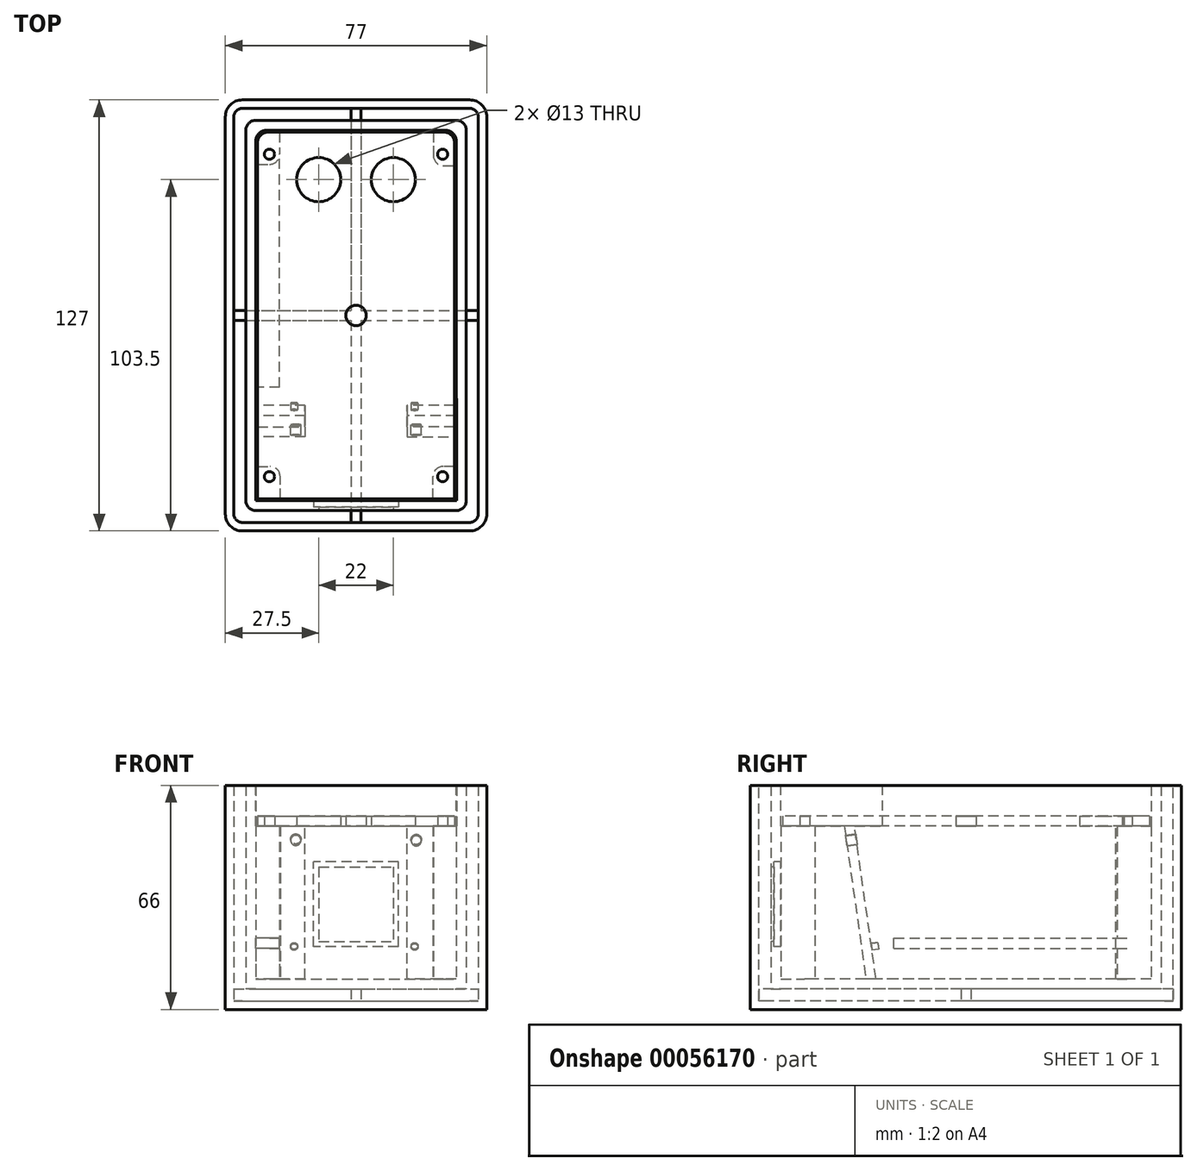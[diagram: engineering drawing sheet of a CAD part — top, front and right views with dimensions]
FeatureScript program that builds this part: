
annotation { "Feature Type Name" : "Feature", "Feature Type Description" : "" }
export const myFeature = defineFeature(function(context is Context, id is Id, definition is map)
    precondition{}
    {
        {
            var Q0;
            Q0=qCreatedBy(makeId("Top.planeOp"),FACE);
            cPlane(context, id + "F0", {"entities" : qUnion([Q0]), "cplaneType" : CPlaneType.OFFSET, "offset" : 6 * mm, "oppositeDirection" : true, "width" : 150 * mm, "height" : 150 * mm});
        }
        {
            var Q0;
            Q0=qCreatedBy(id+"F0.planeOp",FACE);
            var sketch = newSketch(context, id + "F1", { "sketchPlane" : qUnion([Q0])});
            skLineSegment(sketch, "E0.bottom", {"start": v(-33.5, 63.5) * mm, "end": v(33.5, 63.5) * mm});
            skLineSegment(sketch, "E0.top", {"start": v(-33.5, -63.5) * mm, "end": v(33.5, -63.5) * mm});
            skLineSegment(sketch, "E0.left", {"start": v(-38.5, 58.5) * mm, "end": v(-38.5, -58.5) * mm});
            skLineSegment(sketch, "E0.right", {"start": v(38.5, 58.5) * mm, "end": v(38.5, -58.5) * mm});
            skPoint(sketch, "E1.visualSharp", {"position": v(-38.5, 63.5) * mm});
            skArc(sketch, "E1.filletArc", {"start": v(-33.5, 63.5) * mm, "mid": v(-37.04, 62.04) * mm, "end": v(-38.5, 58.5) * mm});
            skPoint(sketch, "E2.visualSharp", {"position": v(38.5, 63.5) * mm});
            skArc(sketch, "E2.filletArc", {"start": v(38.5, 58.5) * mm, "mid": v(37.04, 62.04) * mm, "end": v(33.5, 63.5) * mm});
            skPoint(sketch, "E3.visualSharp", {"position": v(38.5, -63.5) * mm});
            skArc(sketch, "E3.filletArc", {"start": v(33.5, -63.5) * mm, "mid": v(37.04, -62.04) * mm, "end": v(38.5, -58.5) * mm});
            skPoint(sketch, "E4.visualSharp", {"position": v(-38.5, -63.5) * mm});
            skArc(sketch, "E4.filletArc", {"start": v(-38.5, -58.5) * mm, "mid": v(-37.04, -62.04) * mm, "end": v(-33.5, -63.5) * mm});
            skSolve(sketch);
        }
        {
            var Q0;
            Q0 = qSketchRegion(id + "F1", true);
            extrude(context, id + "F2", {"entities" : qUnion([Q0]), "depth" : 66 * mm});
        }
        {
            var Q0;
            Q0=makeQuery(id+"F2.opExtrude","CAP_FACE",FACE,{"disambiguationData":[OSD([sQuery(id+"F1.wireOp",EDGE,"E0.bottom"),sQuery(id+"F1.wireOp",EDGE,"E0.top"),sQuery(id+"F1.wireOp",EDGE,"E0.left"),sQuery(id+"F1.wireOp",EDGE,"E0.right"),sQuery(id+"F1.wireOp",EDGE,"E1.filletArc"),sQuery(id+"F1.wireOp",EDGE,"E2.filletArc"),sQuery(id+"F1.wireOp",EDGE,"E3.filletArc"),sQuery(id+"F1.wireOp",EDGE,"E4.filletArc")])],"isStart":false});
            shell(context, id + "F3", {"entities" : qUnion([Q0]), "thickness" : 2.5 * mm});
        }
        {
            var Q0;
            Q0=qCreatedBy(makeId("Top.planeOp"),FACE);
            var sketch = newSketch(context, id + "F4", { "sketchPlane" : qUnion([Q0])});
            skLineSegment(sketch, "E5.bottom", {"start": v(-32.5, 57.5) * mm, "end": v(32.5, 57.5) * mm});
            skLineSegment(sketch, "E5.top", {"start": v(-32.5, -57.5) * mm, "end": v(32.5, -57.5) * mm});
            skLineSegment(sketch, "E5.left", {"start": v(-32.5, 57.5) * mm, "end": v(-32.5, -57.5) * mm});
            skLineSegment(sketch, "E5.right", {"start": v(32.5, 57.5) * mm, "end": v(32.5, -57.5) * mm});
            skSolve(sketch);
        }
        {
            var Q0;
            Q0 = qSketchRegion(id + "F4", true);
            extrude(context, id + "F5", {"entities" : qUnion([Q0]), "depth" : 60 * mm});
        }
        {
            var Q0;
            Q0=makeQuery(id+"F5.opExtrude","CAP_FACE",FACE,{"disambiguationData":[OSD([sQuery(id+"F4.wireOp",EDGE,"E5.bottom"),sQuery(id+"F4.wireOp",EDGE,"E5.top"),sQuery(id+"F4.wireOp",EDGE,"E5.left"),sQuery(id+"F4.wireOp",EDGE,"E5.right")])],"isStart":false});
            shell(context, id + "F6", {"entities" : qUnion([Q0]), "thickness" : 3 * mm});
        }
        {
            var Q0;
            Q0=makeQuery(id+"F6.opShell","OFFSET_EDGE",EDGE,{"disambiguationData":[OSD([sQuery(id+"F4.wireOp",EDGE,"E5.bottom"),sQuery(id+"F4.wireOp",EDGE,"E5.left")])]});
            var Q1;
            Q1=makeQuery(id+"F5.opExtrude","SWEPT_EDGE",EDGE,{"disambiguationData":[OSD([sQuery(id+"F4.wireOp",EDGE,"E5.top"),sQuery(id+"F4.wireOp",EDGE,"E5.right")])]});
            var Q2;
            Q2=makeQuery(id+"F5.opExtrude","SWEPT_EDGE",EDGE,{"disambiguationData":[OSD([sQuery(id+"F4.wireOp",EDGE,"E5.top"),sQuery(id+"F4.wireOp",EDGE,"E5.left")])]});
            var Q3;
            Q3=makeQuery(id+"F5.opExtrude","SWEPT_EDGE",EDGE,{"disambiguationData":[OSD([sQuery(id+"F4.wireOp",EDGE,"E5.bottom"),sQuery(id+"F4.wireOp",EDGE,"E5.right")])]});
            var Q4;
            Q4=makeQuery(id+"F6.opShell","OFFSET_EDGE",EDGE,{"disambiguationData":[OSD([sQuery(id+"F4.wireOp",EDGE,"E5.top"),sQuery(id+"F4.wireOp",EDGE,"E5.right")])]});
            var Q5;
            Q5=makeQuery(id+"F5.opExtrude","SWEPT_EDGE",EDGE,{"disambiguationData":[OSD([sQuery(id+"F4.wireOp",EDGE,"E5.bottom"),sQuery(id+"F4.wireOp",EDGE,"E5.left")])]});
            var Q6;
            Q6=makeQuery(id+"F6.opShell","OFFSET_EDGE",EDGE,{"disambiguationData":[OSD([sQuery(id+"F4.wireOp",EDGE,"E5.bottom"),sQuery(id+"F4.wireOp",EDGE,"E5.right")])]});
            var Q7;
            Q7=makeQuery(id+"F6.opShell","OFFSET_EDGE",EDGE,{"disambiguationData":[OSD([sQuery(id+"F4.wireOp",EDGE,"E5.top"),sQuery(id+"F4.wireOp",EDGE,"E5.left")])]});
            fillet(context, id + "F7", {"entities" : qUnion([Q0, Q1, Q2, Q3, Q4, Q5, Q6, Q7]), "radius" : 3 * mm, "tangentPropagation" : true, "allowEdgeOverflow" : false});
        }
        {
            var Q0;
            Q0=makeQuery(id+"F6.opShell","OFFSET_FACE",FACE,{"disambiguationData":[OSD([sQuery(id+"F4.wireOp",EDGE,"E5.left")])]});
            var sketch = newSketch(context, id + "F8", { "sketchPlane" : qUnion([Q0])});
            skLineSegment(sketch, "E6", {"start": v(-29.5, 3) * mm, "end": v(-37.5, 60) * mm});
            skLineSegment(sketch, "E7", {"start": v(-34.5, 60) * mm, "end": v(-26.5, 3) * mm});
            skLineSegment(sketch, "E8", {"start": v(-37.5, 60) * mm, "end": v(-34.5, 60) * mm});
            skLineSegment(sketch, "E9", {"start": v(-29.5, 3) * mm, "end": v(-26.5, 3) * mm});
            skSolve(sketch);
        }
        {
            var Q0;
            Q0 = qSketchRegion(id + "F8", true);
            extrude(context, id + "F9", {"entities" : qUnion([Q0]), "operationType" : NewBodyOperationType.ADD, "depth" : 60 * mm});
        }
        {
            var Q0;
            Q0=makeQuery(id+"F6.opShell","OFFSET_FACE",FACE,{"disambiguationData":[OSD([sQuery(id+"F4.wireOp",EDGE,"E5.top")])]});
            var sketch = newSketch(context, id + "F10", { "sketchPlane" : qUnion([Q0])});
            skLineSegment(sketch, "E10.bottom", {"start": v(15, 3) * mm, "end": v(-15, 3) * mm});
            skLineSegment(sketch, "E10.left", {"start": v(15, 3) * mm, "end": v(15, 48) * mm});
            skLineSegment(sketch, "E10.right", {"start": v(-15, 3) * mm, "end": v(-15, 48) * mm});
            skLineSegment(sketch, "E11", {"start": v(15, 48) * mm, "end": v(29.53, 48) * mm});
            skLineSegment(sketch, "E12", {"start": v(-15, 48) * mm, "end": v(-29.66, 48) * mm});
            skLineSegment(sketch, "E13", {"start": v(29.53, 48) * mm, "end": v(29.53, 69.17) * mm});
            skLineSegment(sketch, "E14", {"start": v(29.53, 69.17) * mm, "end": v(-29.66, 69.17) * mm});
            skLineSegment(sketch, "E15", {"start": v(-29.66, 69.17) * mm, "end": v(-29.66, 48) * mm});
            skSolve(sketch);
        }
        {
            var Q0;
            Q0 = qSketchRegion(id + "F10", true);
            extrude(context, id + "F11", {"entities" : qUnion([Q0]), "operationType" : NewBodyOperationType.REMOVE, "depth" : 30 * mm});
        }
        {
            var Q0;
            Q0=makeQuery(id+"F5.opExtrude","SWEPT_FACE",FACE,{"disambiguationData":[OSD([sQuery(id+"F4.wireOp",EDGE,"E5.top")])]});
            var sketch = newSketch(context, id + "F12", { "sketchPlane" : qUnion([Q0])});
            skLineSegment(sketch, "E16.bottom", {"start": v(-12.5, 37.5) * mm, "end": v(12.5, 37.5) * mm});
            skLineSegment(sketch, "E16.top", {"start": v(-12.5, 12.5) * mm, "end": v(12.5, 12.5) * mm});
            skLineSegment(sketch, "E16.left", {"start": v(-12.5, 37.5) * mm, "end": v(-12.5, 12.5) * mm});
            skLineSegment(sketch, "E16.right", {"start": v(12.5, 37.5) * mm, "end": v(12.5, 12.5) * mm});
            skSolve(sketch);
        }
        {
            var Q0;
            Q0 = qSketchRegion(id + "F12", true);
            extrude(context, id + "F13", {"entities" : qUnion([Q0]), "operationType" : NewBodyOperationType.REMOVE, "oppositeDirection" : true, "depth" : 25 * mm});
        }
        {
            var Q0;
            Q0=makeQuery(id+"F5.opExtrude","SWEPT_FACE",FACE,{"disambiguationData":[OSD([sQuery(id+"F4.wireOp",EDGE,"E5.top")])]});
            var sketch = newSketch(context, id + "F14", { "sketchPlane" : qUnion([Q0])});
            skLineSegment(sketch, "E17.bottom", {"start": v(-11, 36) * mm, "end": v(11, 36) * mm});
            skLineSegment(sketch, "E17.top", {"start": v(-11, 14) * mm, "end": v(11, 14) * mm});
            skLineSegment(sketch, "E17.left", {"start": v(-11, 36) * mm, "end": v(-11, 14) * mm});
            skLineSegment(sketch, "E17.right", {"start": v(11, 36) * mm, "end": v(11, 14) * mm});
            skLineSegment(sketch, "E18.bottom", {"start": v(-14.77, 39.77) * mm, "end": v(15.56, 39.77) * mm});
            skLineSegment(sketch, "E18.top", {"start": v(-14.77, 9.44) * mm, "end": v(15.56, 9.44) * mm});
            skLineSegment(sketch, "E18.left", {"start": v(-14.77, 39.77) * mm, "end": v(-14.77, 9.44) * mm});
            skLineSegment(sketch, "E18.right", {"start": v(15.56, 39.77) * mm, "end": v(15.56, 9.44) * mm});
            skSolve(sketch);
        }
        {
            var Q0;
            Q0 = qSketchRegion(id + "F14", true);
            extrude(context, id + "F15", {"entities" : qUnion([Q0]), "operationType" : NewBodyOperationType.ADD, "oppositeDirection" : true, "depth" : 1 * mm});
        }
        {
            var Q0;
            {var subQ0=sQuery(id+"F4.wireOp",EDGE,"E5.right");Q0=makeQuery(id+"F11.boolean.opBoolean","SPLIT",FACE,{"disambiguationData":[TD([makeQuery(id+"F6.opShell","OFFSET_FACE",FACE,{"disambiguationData":[OSD([subQ0])]})])],"derivedFrom":makeQuery(id+"F9.opExtrude","SWEPT_FACE",FACE,{"disambiguationData":[OSD([sQuery(id+"F8.wireOp",EDGE,"E7")])]})});}
            var sketch = newSketch(context, id + "F16", { "sketchPlane" : qUnion([Q0])});
            skCircle(sketch, "E19", {"center": v(-17.75, 48.17) * mm, "radius": 1.5 * mm});
            skCircle(sketch, "E20", {"center": v(17.75, 48.3) * mm, "radius": 1.5 * mm});
            skSolve(sketch);
        }
        {
            var Q0;
            Q0 = qSketchRegion(id + "F16", true);
            extrude(context, id + "F17", {"entities" : qUnion([Q0]), "operationType" : NewBodyOperationType.REMOVE, "oppositeDirection" : true, "depth" : 5 * mm});
        }
        {
            var Q0;
            {var subQ0=sQuery(id+"F4.wireOp",EDGE,"E5.right");Q0=makeQuery(id+"F11.boolean.opBoolean","SPLIT",FACE,{"disambiguationData":[TD([makeQuery(id+"F6.opShell","OFFSET_FACE",FACE,{"disambiguationData":[OSD([subQ0])]})])],"derivedFrom":makeQuery(id+"F9.opExtrude","SWEPT_FACE",FACE,{"disambiguationData":[OSD([sQuery(id+"F8.wireOp",EDGE,"E7")])]})});}
            var sketch = newSketch(context, id + "F18", { "sketchPlane" : qUnion([Q0])});
            skCircle(sketch, "E21", {"center": v(-17.25, 16.17) * mm, "radius": 1 * mm});
            skCircle(sketch, "E22", {"center": v(18.25, 16.17) * mm, "radius": 1 * mm});
            skSolve(sketch);
        }
        {
            var Q0;
            Q0 = qSketchRegion(id + "F18", true);
            extrude(context, id + "F19", {"entities" : qUnion([Q0]), "operationType" : NewBodyOperationType.ADD, "depth" : 2 * mm});
        }
        {
            var Q0;
            {var subQ0=sQuery(id+"F4.wireOp",EDGE,"E5.left");Q0=makeQuery(id+"F9.boolean.opBoolean","SPLIT",FACE,{"disambiguationData":[TD([makeQuery(id+"F9.opExtrude","SWEPT_FACE",FACE,{"disambiguationData":[OSD([sQuery(id+"F8.wireOp",EDGE,"E7")])]})])],"derivedFrom":makeQuery(id+"F6.opShell","OFFSET_FACE",FACE,{"disambiguationData":[OSD([subQ0])]})});}
            var sketch = newSketch(context, id + "F20", { "sketchPlane" : qUnion([Q0])});
            skLineSegment(sketch, "E23.bottom", {"start": v(-21.22, 12) * mm, "end": v(54.68, 12) * mm});
            skLineSegment(sketch, "E23.top", {"start": v(-21.22, 15.08) * mm, "end": v(54.68, 15.08) * mm});
            skLineSegment(sketch, "E23.left", {"start": v(-21.22, 12) * mm, "end": v(-21.22, 15.08) * mm});
            skLineSegment(sketch, "E23.right", {"start": v(54.68, 12) * mm, "end": v(54.68, 15.08) * mm});
            skSolve(sketch);
        }
        {
            var Q0;
            Q0 = qSketchRegion(id + "F20", true);
            extrude(context, id + "F21", {"entities" : qUnion([Q0]), "operationType" : NewBodyOperationType.ADD, "depth" : 7 * mm});
        }
        {
            var Q0;
            {var subQ0=sQuery(id+"F4.wireOp",EDGE,"E5.left");var subQ1=sQuery(id+"F4.wireOp",EDGE,"E5.top");var subQ2=sQuery(id+"F4.wireOp",EDGE,"E5.right");var subQ5=sQuery(id+"F4.wireOp",EDGE,"E5.bottom");var subQ6=makeQuery(id+"F6.opShell","OFFSET_FACE",FACE,{"disambiguationData":[OSD([subQ5,subQ1,subQ0,subQ2])]});Q0=makeQuery(id+"F11.boolean.opBoolean","MERGE",FACE,{"derivedFrom":[makeQuery(id+"F9.boolean.opBoolean","SPLIT",FACE,{"disambiguationData":[TD([makeQuery(id+"F6.opShell","OFFSET_FACE",FACE,{"disambiguationData":[OSD([subQ5])]})])],"derivedFrom":subQ6}),makeQuery(id+"F9.boolean.opBoolean","SPLIT",FACE,{"disambiguationData":[TD([makeQuery(id+"F6.opShell","OFFSET_FACE",FACE,{"disambiguationData":[OSD([subQ1])]})])],"derivedFrom":subQ6}),makeQuery(id+"F11.opExtrude","SWEPT_FACE",FACE,{"disambiguationData":[OSD([sQuery(id+"F10.wireOp",EDGE,"E10.bottom")])]})]});}
            var sketch = newSketch(context, id + "F22", { "sketchPlane" : qUnion([Q0])});
            skLineSegment(sketch, "E24.bottom", {"start": v(-29.5, 54.5) * mm, "end": v(-22.5, 54.5) * mm});
            skLineSegment(sketch, "E24.top", {"start": v(-29.5, 44.5) * mm, "end": v(-25.5, 44.5) * mm});
            skLineSegment(sketch, "E24.left", {"start": v(-29.5, 54.5) * mm, "end": v(-29.5, 44.5) * mm});
            skLineSegment(sketch, "E24.right", {"start": v(-22.5, 54.5) * mm, "end": v(-22.5, 47.5) * mm});
            skLineSegment(sketch, "E25.bottom", {"start": v(22.75, 54.5) * mm, "end": v(29.75, 54.5) * mm});
            skLineSegment(sketch, "E25.top", {"start": v(25.75, 44.16) * mm, "end": v(29.75, 44.16) * mm});
            skLineSegment(sketch, "E25.left", {"start": v(22.75, 54.5) * mm, "end": v(22.75, 47.16) * mm});
            skLineSegment(sketch, "E25.right", {"start": v(29.75, 54.5) * mm, "end": v(29.75, 44.16) * mm});
            skLineSegment(sketch, "E26.bottom", {"start": v(-29.5, -54.5) * mm, "end": v(-22.35, -54.5) * mm});
            skLineSegment(sketch, "E26.top", {"start": v(-29.5, -44.5) * mm, "end": v(-25.35, -44.5) * mm});
            skLineSegment(sketch, "E26.left", {"start": v(-29.5, -54.5) * mm, "end": v(-29.5, -44.5) * mm});
            skLineSegment(sketch, "E26.right", {"start": v(-22.35, -54.5) * mm, "end": v(-22.35, -47.5) * mm});
            skLineSegment(sketch, "E27.bottom", {"start": v(29.66, -54.5) * mm, "end": v(22.66, -54.5) * mm});
            skLineSegment(sketch, "E27.top", {"start": v(29.66, -44.5) * mm, "end": v(25.66, -44.5) * mm});
            skLineSegment(sketch, "E27.left", {"start": v(29.66, -54.5) * mm, "end": v(29.66, -44.5) * mm});
            skLineSegment(sketch, "E27.right", {"start": v(22.66, -54.5) * mm, "end": v(22.66, -47.5) * mm});
            skPoint(sketch, "E28.visualSharp", {"position": v(-22.5, 44.5) * mm});
            skArc(sketch, "E28.filletArc", {"start": v(-25.5, 44.5) * mm, "mid": v(-23.38, 45.38) * mm, "end": v(-22.5, 47.5) * mm});
            skPoint(sketch, "E29.visualSharp", {"position": v(22.75, 44.16) * mm});
            skArc(sketch, "E29.filletArc", {"start": v(22.75, 47.16) * mm, "mid": v(23.63, 45.04) * mm, "end": v(25.75, 44.16) * mm});
            skPoint(sketch, "E30.visualSharp", {"position": v(22.66, -44.5) * mm});
            skArc(sketch, "E30.filletArc", {"start": v(25.66, -44.5) * mm, "mid": v(23.54, -45.38) * mm, "end": v(22.66, -47.5) * mm});
            skPoint(sketch, "E31.visualSharp", {"position": v(-22.35, -44.5) * mm});
            skArc(sketch, "E31.filletArc", {"start": v(-22.35, -47.5) * mm, "mid": v(-23.23, -45.38) * mm, "end": v(-25.35, -44.5) * mm});
            skSolve(sketch);
        }
        {
            var Q0;
            Q0 = qSketchRegion(id + "F22", true);
            extrude(context, id + "F23", {"entities" : qUnion([Q0]), "operationType" : NewBodyOperationType.ADD, "depth" : 45 * mm});
        }
        {
            var Q0;
            Q0=makeQuery(id+"F23.opExtrude","CAP_FACE",FACE,{"disambiguationData":[OSD([sQuery(id+"F22.wireOp",EDGE,"E24.bottom"),sQuery(id+"F22.wireOp",EDGE,"E24.top"),sQuery(id+"F22.wireOp",EDGE,"E24.left"),sQuery(id+"F22.wireOp",EDGE,"E24.right"),sQuery(id+"F22.wireOp",EDGE,"E28.filletArc")])],"isStart":false});
            var sketch = newSketch(context, id + "F24", { "sketchPlane" : qUnion([Q0])});
            skLineSegment(sketch, "E32.bottom", {"start": v(-26, 54) * mm, "end": v(26, 54) * mm});
            skLineSegment(sketch, "E32.top", {"start": v(-29, -54) * mm, "end": v(29, -54) * mm});
            skLineSegment(sketch, "E32.left", {"start": v(-29, 51) * mm, "end": v(-29, -54) * mm});
            skLineSegment(sketch, "E32.right", {"start": v(29, 51) * mm, "end": v(29, -54) * mm});
            skPoint(sketch, "E33.visualSharp", {"position": v(-29, 54) * mm});
            skArc(sketch, "E33.filletArc", {"start": v(-26, 54) * mm, "mid": v(-28.12, 53.12) * mm, "end": v(-29, 51) * mm});
            skPoint(sketch, "E34.visualSharp", {"position": v(29, 54) * mm});
            skArc(sketch, "E34.filletArc", {"start": v(29, 51) * mm, "mid": v(28.12, 53.12) * mm, "end": v(26, 54) * mm});
            skCircle(sketch, "E35", {"center": v(-25.5, 47.5) * mm, "radius": 1.5 * mm});
            skCircle(sketch, "E36", {"center": v(25.5, -47.5) * mm, "radius": 1.5 * mm});
            skCircle(sketch, "E37", {"center": v(25.5, 47.5) * mm, "radius": 1.5 * mm});
            skCircle(sketch, "E38", {"center": v(-25.5, -47.5) * mm, "radius": 1.5 * mm});
            skCircle(sketch, "E39", {"center": v(-11, 40) * mm, "radius": 6.5 * mm});
            skCircle(sketch, "E40", {"center": v(11, 40) * mm, "radius": 6.5 * mm});
            skCircle(sketch, "E41", {"center": v(0, 0) * mm, "radius": 3 * mm});
            skSolve(sketch);
        }
        {
            var Q0;
            Q0 = qSketchRegion(id + "F24", true);
            extrude(context, id + "F25", {"entities" : qUnion([Q0]), "depth" : 3 * mm});
        }
        {
            var Q0;
            Q0=makeQuery(id+"F3.opShell","OFFSET_FACE",FACE,{"disambiguationData":[OSD([sQuery(id+"F1.wireOp",EDGE,"E0.bottom"),sQuery(id+"F1.wireOp",EDGE,"E0.top"),sQuery(id+"F1.wireOp",EDGE,"E0.left"),sQuery(id+"F1.wireOp",EDGE,"E0.right"),sQuery(id+"F1.wireOp",EDGE,"E1.filletArc"),sQuery(id+"F1.wireOp",EDGE,"E2.filletArc"),sQuery(id+"F1.wireOp",EDGE,"E3.filletArc"),sQuery(id+"F1.wireOp",EDGE,"E4.filletArc")])]});
            var sketch = newSketch(context, id + "F26", { "sketchPlane" : qUnion([Q0])});
            skLineSegment(sketch, "E42.bottom", {"start": v(-1.5, 61) * mm, "end": v(1.5, 61) * mm});
            skLineSegment(sketch, "E42.top", {"start": v(-1.5, -61) * mm, "end": v(1.5, -61) * mm});
            skLineSegment(sketch, "E42.left", {"start": v(-1.5, 61) * mm, "end": v(-1.5, -61) * mm});
            skLineSegment(sketch, "E42.right", {"start": v(1.5, 61) * mm, "end": v(1.5, -61) * mm});
            skLineSegment(sketch, "E43.bottom", {"start": v(-36, 1.5) * mm, "end": v(36, 1.5) * mm});
            skLineSegment(sketch, "E43.top", {"start": v(-36, -1.5) * mm, "end": v(36, -1.5) * mm});
            skLineSegment(sketch, "E43.left", {"start": v(-36, 1.5) * mm, "end": v(-36, -1.5) * mm});
            skLineSegment(sketch, "E43.right", {"start": v(36, 1.5) * mm, "end": v(36, -1.5) * mm});
            skSolve(sketch);
        }
        {
            var Q0;
            Q0 = qSketchRegion(id + "F26", true);
            extrude(context, id + "F27", {"entities" : qUnion([Q0]), "depth" : 3.5 * mm});
        }
    });
